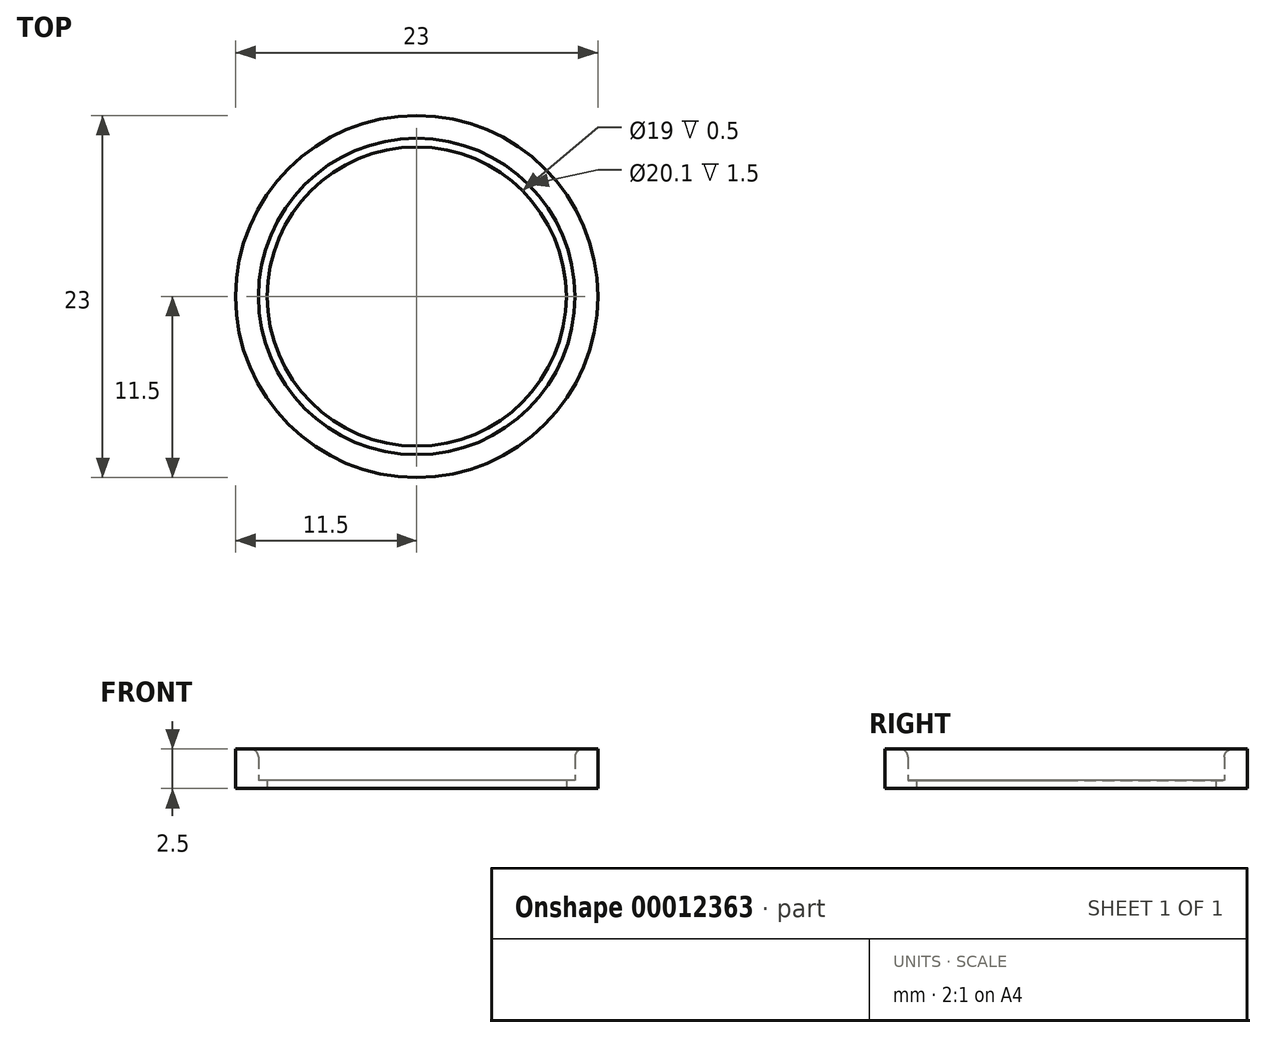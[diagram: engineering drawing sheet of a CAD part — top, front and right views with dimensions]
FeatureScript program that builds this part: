
annotation { "Feature Type Name" : "Feature", "Feature Type Description" : "" }
export const myFeature = defineFeature(function(context is Context, id is Id, definition is map)
    precondition{}
    {
        {
            var Q0;
            Q0=qCreatedBy(makeId("Top.planeOp"),FACE);
            var sketch = newSketch(context, id + "F0", { "sketchPlane" : qUnion([Q0])});
            skCircle(sketch, "E0", {"center": v(0, 0) * mm, "radius": 10.05 * mm});
            skCircle(sketch, "E1", {"center": v(0, 0) * mm, "radius": 11.5 * mm});
            skCircle(sketch, "E2", {"center": v(0, 0) * mm, "radius": 9.5 * mm});
            skSolve(sketch);
        }
        {
            var Q0;
            Q0=makeQuery(id+"F0.imprint","IMPRINT",FACE,{"disambiguationData":[TD([[makeQuery(id+"F0.imprint","IMPRINT",EDGE,{"derivedFrom":sQuery(id+"F0.wireOp",EDGE,"E0")}),1.0]])]});
            extrude(context, id + "F1", {"entities" : qUnion([Q0]), "depth" : 0.5 * mm});
        }
        {
            var Q0;
            Q0=makeQuery(id+"F0.imprint","IMPRINT",FACE,{"disambiguationData":[TD([[makeQuery(id+"F0.imprint","IMPRINT",EDGE,{"derivedFrom":sQuery(id+"F0.wireOp",EDGE,"E0")}),-1.0]])]});
            extrude(context, id + "F2", {"entities" : qUnion([Q0]), "operationType" : NewBodyOperationType.ADD, "depth" : 2.5 * mm});
        }
        {
            var Q0;
            Q0=makeQuery(id+"F2.opExtrude","CAP_EDGE",EDGE,{"disambiguationData":[OSD([sQuery(id+"F0.wireOp",EDGE,"E0")])],"isStart":false});
            fillet(context, id + "F3", {"entities" : qUnion([Q0]), "radius" : 0.5 * mm, "tangentPropagation" : true, "allowEdgeOverflow" : false});
        }
    });
